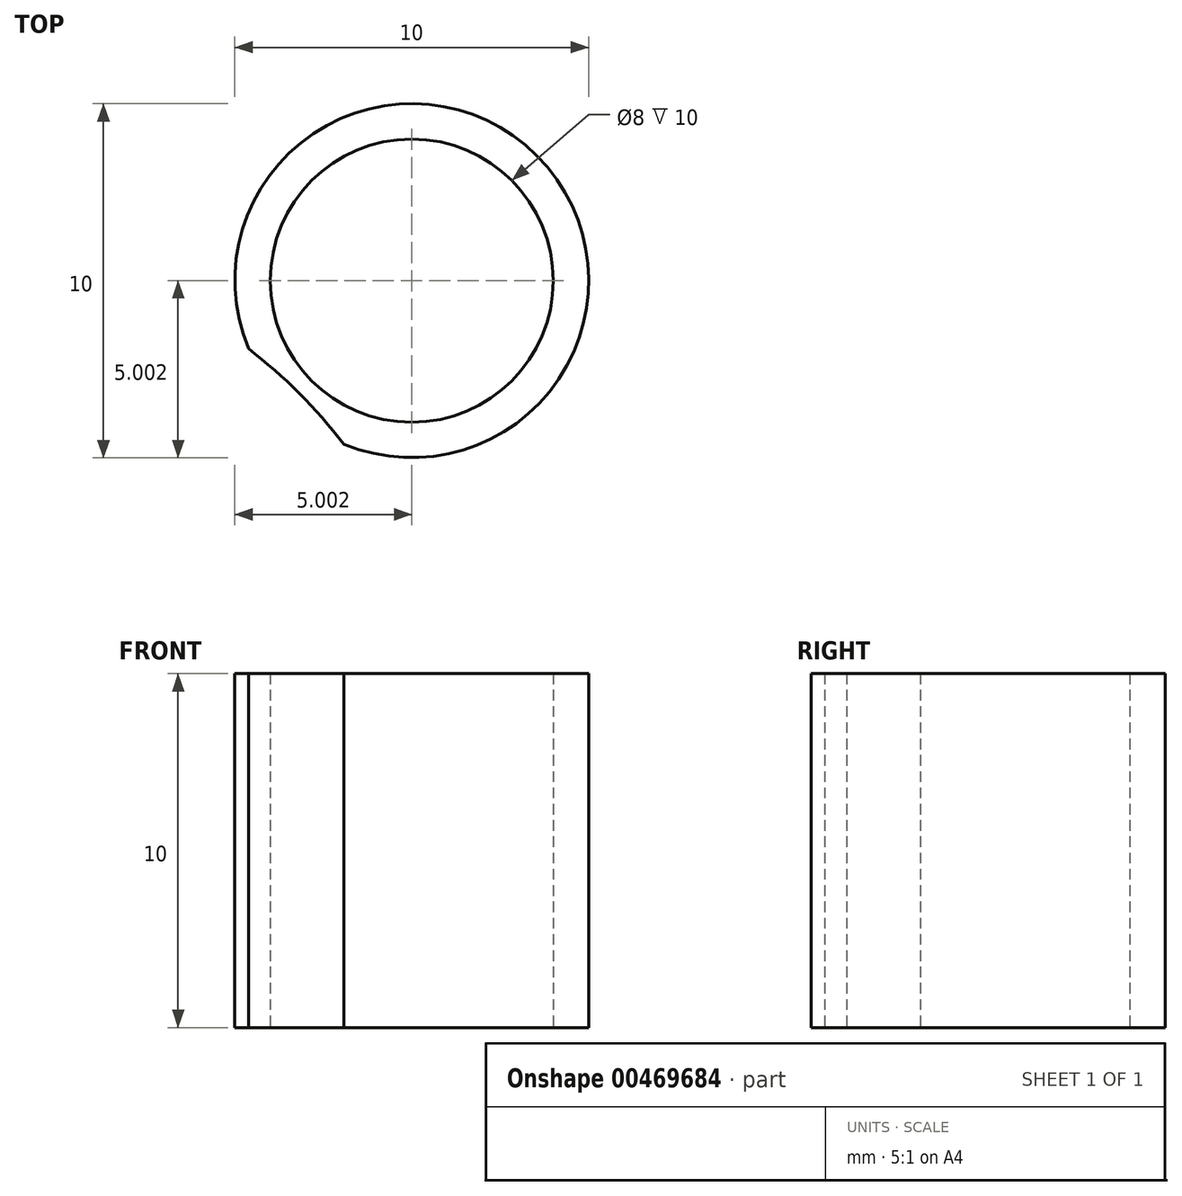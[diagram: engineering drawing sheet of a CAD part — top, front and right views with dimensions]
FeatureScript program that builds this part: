
annotation { "Feature Type Name" : "Feature", "Feature Type Description" : "" }
export const myFeature = defineFeature(function(context is Context, id is Id, definition is map)
    precondition{}
    {
        {
            var Q0;
            Q0=qCreatedBy(makeId("Top.planeOp"),FACE);
            var sketch = newSketch(context, id + "F0", { "sketchPlane" : qUnion([Q0])});
            skCircle(sketch, "E0", {"center": v(0.01, 0.4) * mm, "radius": 4 * mm});
            skArc(sketch, "E1", {"start": v(-1.9, -4.23) * mm, "mid": v(3.55, 3.93) * mm, "end": v(-4.6, -1.53) * mm});
            skLineSegment(sketch, "E2", {"start": v(0, 0) * mm, "end": v(0, -19.5) * mm, "construction": true});
            skArc(sketch, "E3", {"start": v(-1.9, -4.23) * mm, "mid": v(-3.17, -2.8) * mm, "end": v(-4.6, -1.53) * mm});
            skSolve(sketch);
        }
        {
            var Q0;
            Q0=makeQuery(id+"F0.imprint","IMPRINT",FACE,{"disambiguationData":[TD([[makeQuery(id+"F0.imprint","IMPRINT",EDGE,{"derivedFrom":sQuery(id+"F0.wireOp",EDGE,"E0")}),-1.0]])]});
            extrude(context, id + "F1", {"entities" : qUnion([Q0]), "depth" : 10 * mm});
        }
    });
